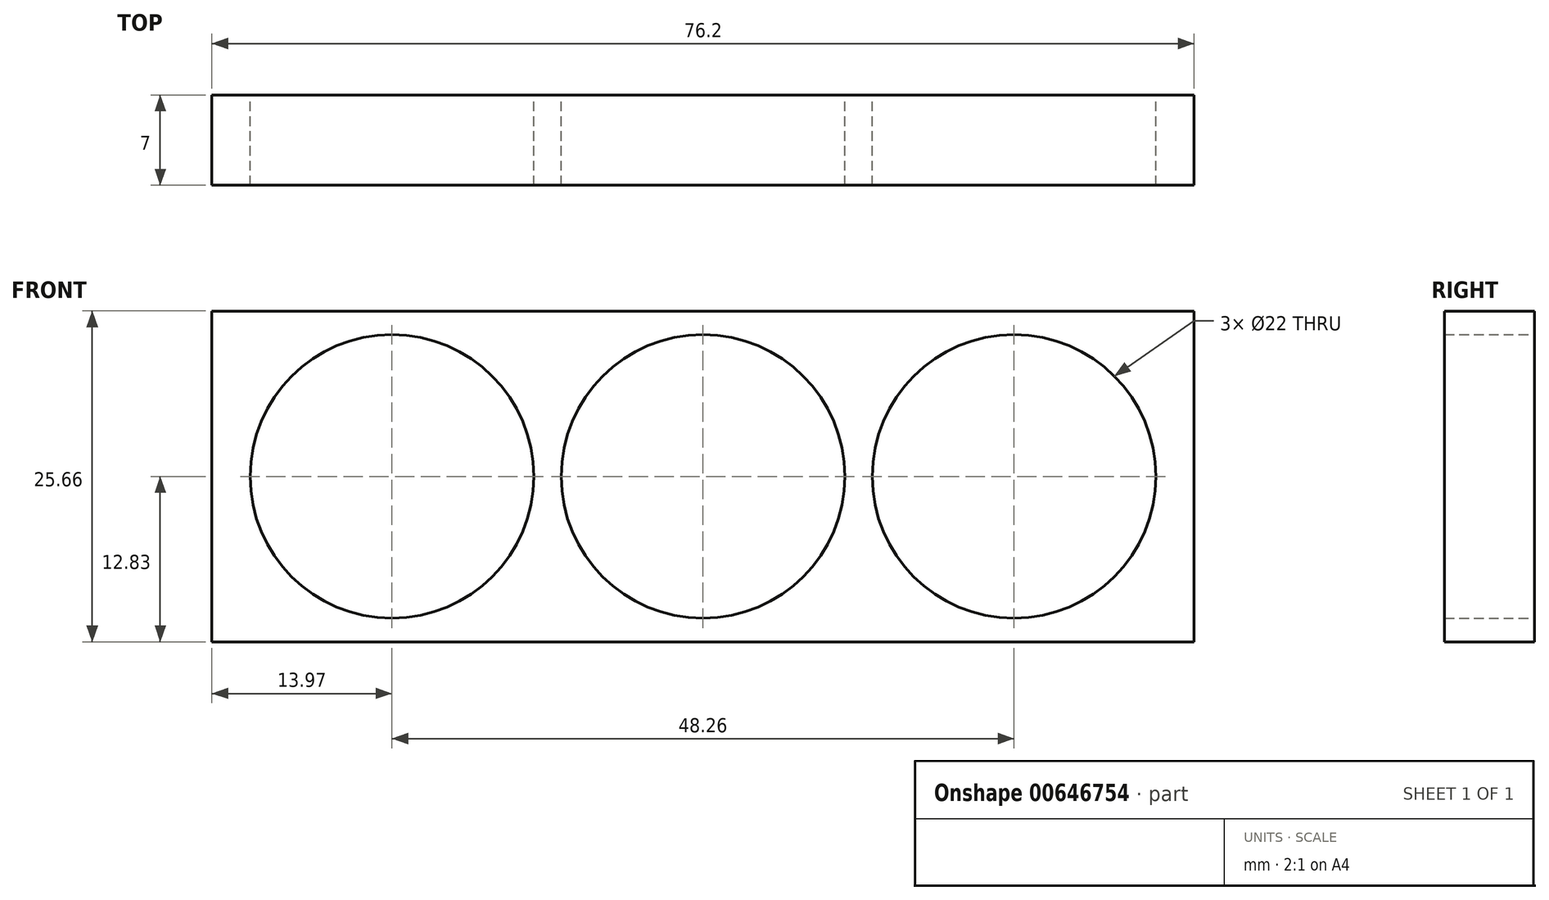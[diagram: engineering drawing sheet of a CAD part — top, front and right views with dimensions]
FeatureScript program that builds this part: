
annotation { "Feature Type Name" : "Feature", "Feature Type Description" : "" }
export const myFeature = defineFeature(function(context is Context, id is Id, definition is map)
    precondition{}
    {
        {
            var Q0;
            Q0=qCreatedBy(makeId("Front.planeOp"),FACE);
            var sketch = newSketch(context, id + "F0", { "sketchPlane" : qUnion([Q0])});
            skLineSegment(sketch, "E0.bottom", {"start": v(-38.1, -12.83) * mm, "end": v(38.1, -12.83) * mm});
            skLineSegment(sketch, "E0.top", {"start": v(-38.1, 12.83) * mm, "end": v(38.1, 12.83) * mm});
            skLineSegment(sketch, "E0.left", {"start": v(-38.1, -12.83) * mm, "end": v(-38.1, 12.83) * mm});
            skLineSegment(sketch, "E0.right", {"start": v(38.1, -12.83) * mm, "end": v(38.1, 12.83) * mm});
            skCircle(sketch, "E1", {"center": v(0, 0) * mm, "radius": 11 * mm});
            skCircle(sketch, "E2", {"center": v(-24.13, 0) * mm, "radius": 11 * mm});
            skCircle(sketch, "E3", {"center": v(24.13, 0) * mm, "radius": 11 * mm});
            skSolve(sketch);
        }
        {
            var Q0;
            Q0=makeQuery(id+"F0.imprint","IMPRINT",FACE,{"disambiguationData":[TD([[makeQuery(id+"F0.imprint","IMPRINT",EDGE,{"derivedFrom":sQuery(id+"F0.wireOp",EDGE,"E0.bottom")}),1.0]])]});
            extrude(context, id + "F1", {"entities" : qUnion([Q0]), "depth" : 7 * mm, "offsetDistance" : 25.4 * mm});
        }
    });
